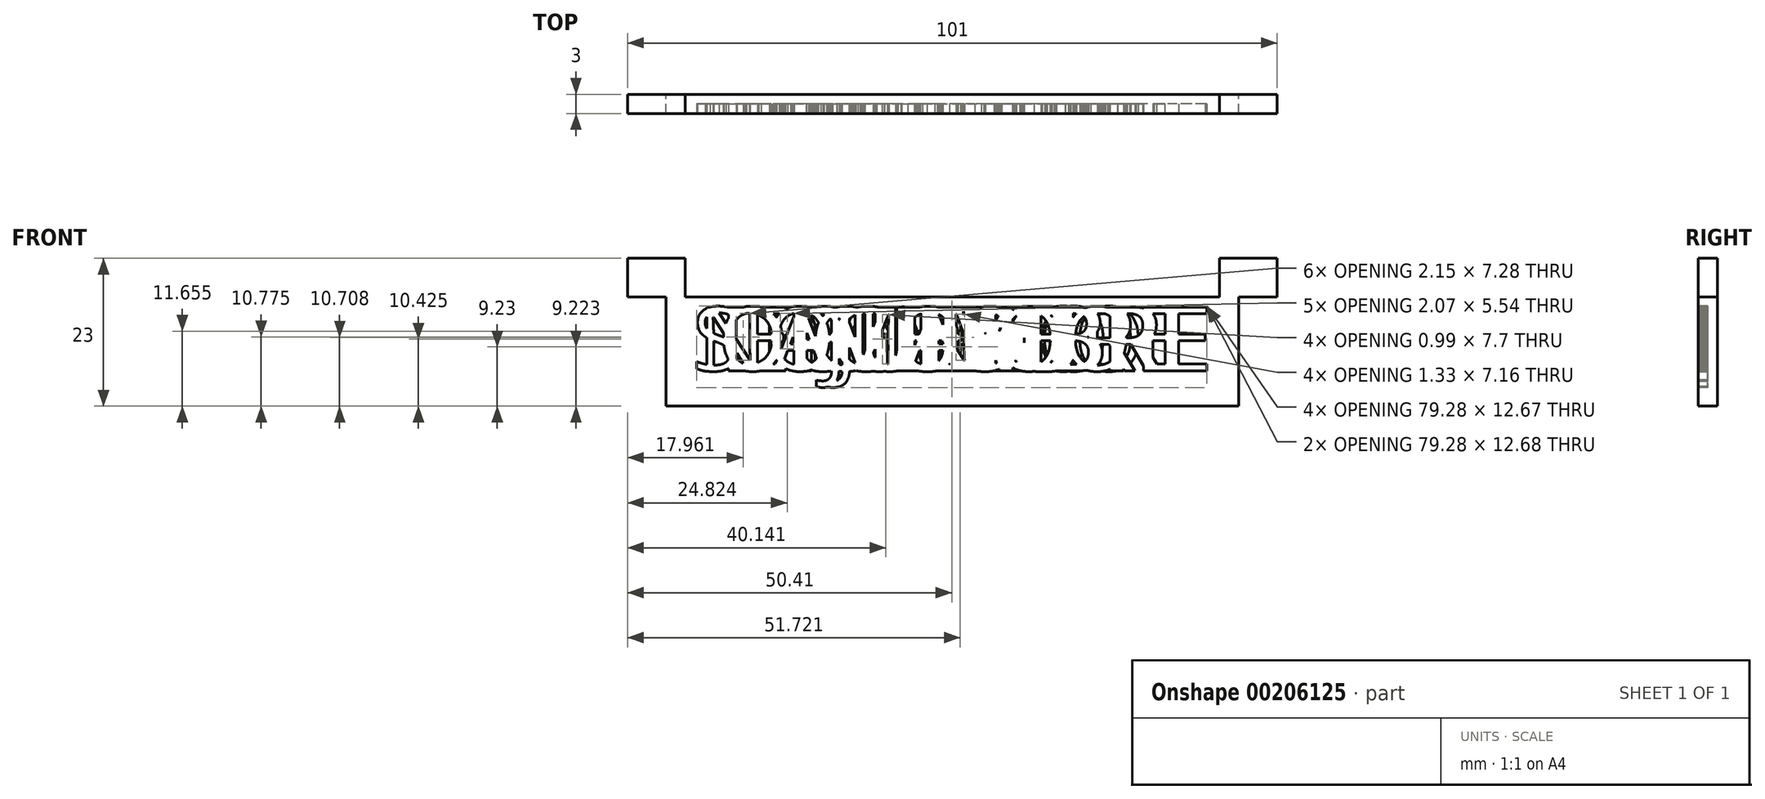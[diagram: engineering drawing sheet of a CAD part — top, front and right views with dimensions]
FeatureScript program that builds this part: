
annotation { "Feature Type Name" : "Feature", "Feature Type Description" : "" }
export const myFeature = defineFeature(function(context is Context, id is Id, definition is map)
    precondition{}
    {
        {
            var Q0;
            Q0=qCreatedBy(makeId("Front.planeOp"),FACE);
            var sketch = newSketch(context, id + "F0", { "sketchPlane" : qUnion([Q0])});
            skLineSegment(sketch, "E0.bottom", {"start": v(-51.5, 23) * mm, "end": v(-42.5, 23) * mm});
            skLineSegment(sketch, "E0.top", {"start": v(-45.5, 0) * mm, "end": v(43.5, 0) * mm});
            skLineSegment(sketch, "E0.left", {"start": v(-51.5, 23) * mm, "end": v(-51.5, 17) * mm});
            skLineSegment(sketch, "E0.right", {"start": v(49.5, 23) * mm, "end": v(49.5, 17) * mm});
            skLineSegment(sketch, "E1.top", {"start": v(-51.5, 17) * mm, "end": v(-45.5, 17) * mm});
            skLineSegment(sketch, "E1.right", {"start": v(-45.5, 0) * mm, "end": v(-45.5, 17) * mm});
            skLineSegment(sketch, "E2.bottom", {"start": v(-51.5, 23) * mm, "end": v(-42.5, 23) * mm, "construction": true});
            skLineSegment(sketch, "E2.top", {"start": v(-51.5, 17) * mm, "end": v(-42.5, 17) * mm, "construction": true});
            skLineSegment(sketch, "E2.left", {"start": v(-51.5, 23) * mm, "end": v(-51.5, 17) * mm, "construction": true});
            skLineSegment(sketch, "E2.right", {"start": v(-42.5, 23) * mm, "end": v(-42.5, 17) * mm, "construction": true});
            skLineSegment(sketch, "E3.top", {"start": v(-42.5, 17) * mm, "end": v(40.5, 17) * mm});
            skLineSegment(sketch, "E3.left", {"start": v(-42.5, 23) * mm, "end": v(-42.5, 17) * mm});
            skLineSegment(sketch, "E3.right", {"start": v(40.5, 23) * mm, "end": v(40.5, 17) * mm});
            skLineSegment(sketch, "E4.top", {"start": v(49.5, 17) * mm, "end": v(43.5, 17) * mm});
            skLineSegment(sketch, "E4.right", {"start": v(43.5, 0) * mm, "end": v(43.5, 17) * mm});
            skLineSegment(sketch, "E5.trimOffspring", {"start": v(40.5, 23) * mm, "end": v(49.5, 23) * mm});
            skSolve(sketch);
        }
        {
            var Q0;
            Q0=makeQuery(id+"F0.imprint","IMPRINT",FACE,{"disambiguationData":[TD([[makeQuery(id+"F0.imprint","IMPRINT",EDGE,{"derivedFrom":sQuery(id+"F0.wireOp",EDGE,"E0.bottom")}),-1.0]])]});
            extrude(context, id + "F1", {"entities" : qUnion([Q0]), "depth" : 3 * mm});
        }
        {
            var Q0;
            Q0=makeQuery(id+"F1.opExtrude","CAP_FACE",FACE,{"disambiguationData":[OSD([sQuery(id+"F0.wireOp",EDGE,"E0.bottom"),sQuery(id+"F0.wireOp",EDGE,"E0.top"),sQuery(id+"F0.wireOp",EDGE,"E0.left"),sQuery(id+"F0.wireOp",EDGE,"E0.right"),sQuery(id+"F0.wireOp",EDGE,"E1.top"),sQuery(id+"F0.wireOp",EDGE,"E1.right"),sQuery(id+"F0.wireOp",EDGE,"E3.top"),sQuery(id+"F0.wireOp",EDGE,"E3.left"),sQuery(id+"F0.wireOp",EDGE,"E3.right"),sQuery(id+"F0.wireOp",EDGE,"E4.top"),sQuery(id+"F0.wireOp",EDGE,"E4.right"),sQuery(id+"F0.wireOp",EDGE,"E5.trimOffspring")])],"isStart":false});
            var sketch = newSketch(context, id + "F2", { "sketchPlane" : qUnion([Q0])});
            skLineSegment(sketch, "E6.0", {"start": v(-45.5, 3.5) * mm, "end": v(-42, 3.5) * mm, "construction": true});
            skLineSegment(sketch, "E7.0", {"start": v(-42, 15.5) * mm, "end": v(40, 15.5) * mm, "construction": true});
            skLineSegment(sketch, "E8.0", {"start": v(-42, 0) * mm, "end": v(-42, 15.5) * mm, "construction": true});
            skText(sketch, "E9", { "text": "ENERO", "fontName": "OpenSans-Regular.ttf"});
            skLineSegment(sketch, "E10.top", {"start": v(-45.5, 0) * mm, "end": v(-42, 0) * mm, "construction": true});
            skLineSegment(sketch, "E10.left", {"start": v(-45.5, 3.5) * mm, "end": v(-45.5, 0) * mm, "construction": true});
            skLineSegment(sketch, "E10.right", {"start": v(-42, 3.5) * mm, "end": v(-42, 0) * mm, "construction": true});
            skLineSegment(sketch, "E11.0", {"start": v(40, 0) * mm, "end": v(40, 17) * mm, "construction": true});
            skPoint(sketch, "E12.orphan", {"position": v(40, 15.5) * mm});
            skPoint(sketch, "E13.end.orphan", {"position": v(-1, 0) * mm});
            skLineSegment(sketch, "E14", {"start": v(-1, 17) * mm, "end": v(-1, 0) * mm, "construction": true});
            const initialGuessF2  = {"E9": [-0.02369, 0.0055, 1, 0, 0.01]};
            skSetInitialGuess(sketch, initialGuessF2);
            skSolve(sketch);
        }
        {
            var Q0;
            Q0=makeQuery(id+"F2.imprint","IMPRINT",FACE,{"disambiguationData":[TD([[makeQuery(id+"F2.imprint","IMPRINT",EDGE,{"derivedFrom":sQuery(id+"F2.wireOp",EDGE,"E9.sketch_text.stroke-0")}),-1.0]])]});
            var Q1;
            Q1=makeQuery(id+"F2.imprint","IMPRINT",FACE,{"disambiguationData":[TD([[makeQuery(id+"F2.imprint","IMPRINT",EDGE,{"derivedFrom":sQuery(id+"F2.wireOp",EDGE,"E9.sketch_text.stroke-10")}),-1.0]])]});
            var Q2;
            Q2=makeQuery(id+"F2.imprint","IMPRINT",FACE,{"disambiguationData":[TD([[makeQuery(id+"F2.imprint","IMPRINT",EDGE,{"derivedFrom":sQuery(id+"F2.wireOp",EDGE,"E9.sketch_text.stroke-23")}),-1.0]])]});
            var Q3;
            Q3=makeQuery(id+"F2.imprint","IMPRINT",FACE,{"disambiguationData":[TD([[makeQuery(id+"F2.imprint","IMPRINT",EDGE,{"derivedFrom":sQuery(id+"F2.wireOp",EDGE,"E9.sketch_text.stroke-38")}),-1.0]])]});
            var Q4;
            Q4=makeQuery(id+"F2.imprint","IMPRINT",FACE,{"disambiguationData":[TD([[makeQuery(id+"F2.imprint","IMPRINT",EDGE,{"derivedFrom":sQuery(id+"F2.wireOp",EDGE,"E9.sketch_text.stroke-52")}),-1.0]])]});
            var Q5;
            Q5=makeQuery(id+"F2.imprint","IMPRINT",FACE,{"disambiguationData":[TD([[makeQuery(id+"F2.imprint","IMPRINT",EDGE,{"derivedFrom":sQuery(id+"F2.wireOp",EDGE,"E9.sketch_text.stroke-65")}),-1.0]])]});
            var Q6;
            Q6=makeQuery(id+"F2.imprint","IMPRINT",FACE,{"disambiguationData":[TD([[makeQuery(id+"F2.imprint","IMPRINT",EDGE,{"derivedFrom":sQuery(id+"F2.wireOp",EDGE,"E9.sketch_text.stroke-83")}),-1.0]])]});
            extrude(context, id + "F3", {"entities" : qUnion([Q0, Q1, Q2, Q3, Q4, Q5, Q6]), "operationType" : NewBodyOperationType.REMOVE, "oppositeDirection" : true, "depth" : 1.5 * mm});
        }
        {
            var Q0;
            Q0=qSketchRegion(id+"F0",true);
            extrude(context, id + "F4", {"entities" : qUnion([Q0]), "depth" : 3 * mm});
        }
        {
            var Q0;
            Q0=makeQuery(id+"F4.opExtrude","CAP_FACE",FACE,{"disambiguationData":[OSD([sQuery(id+"F0.wireOp",EDGE,"E0.bottom"),sQuery(id+"F0.wireOp",EDGE,"E0.top"),sQuery(id+"F0.wireOp",EDGE,"E0.left"),sQuery(id+"F0.wireOp",EDGE,"E0.right"),sQuery(id+"F0.wireOp",EDGE,"E1.top"),sQuery(id+"F0.wireOp",EDGE,"E1.right"),sQuery(id+"F0.wireOp",EDGE,"E3.top"),sQuery(id+"F0.wireOp",EDGE,"E3.left"),sQuery(id+"F0.wireOp",EDGE,"E3.right"),sQuery(id+"F0.wireOp",EDGE,"E4.top"),sQuery(id+"F0.wireOp",EDGE,"E4.right"),sQuery(id+"F0.wireOp",EDGE,"E5.trimOffspring")])],"isStart":false});
            var sketch = newSketch(context, id + "F5", { "sketchPlane" : qUnion([Q0])});
            skText(sketch, "E15", { "text": "FEBRERO", "fontName": "OpenSans-Regular.ttf"});
            skPoint(sketch, "E16.orphan", {"position": v(40.22, 15.5) * mm});
            skPoint(sketch, "E17.end.orphan", {"position": v(-0.5, 0) * mm});
            skPoint(sketch, "E18.orphan", {"position": v(-42.22, 15.5) * mm});
            skLineSegment(sketch, "E19.0", {"start": v(-43.5, 15.5) * mm, "end": v(41.5, 15.5) * mm, "construction": true});
            skPoint(sketch, "E20.start.orphan", {"position": v(-1, 17) * mm});
            const initialGuessF5  = {"E15": [-0.03083, 0.0055, 1, 0, 0.01]};
            skSetInitialGuess(sketch, initialGuessF5);
            skSolve(sketch);
        }
        {
            var Q0;
            Q0=makeQuery(id+"F5.imprint","IMPRINT",FACE,{"disambiguationData":[TD([[makeQuery(id+"F5.imprint","IMPRINT",EDGE,{"derivedFrom":sQuery(id+"F5.wireOp",EDGE,"E15.sketch_text.stroke-0")}),-1.0]])]});
            var Q1;
            Q1=makeQuery(id+"F5.imprint","IMPRINT",FACE,{"disambiguationData":[TD([[makeQuery(id+"F5.imprint","IMPRINT",EDGE,{"derivedFrom":sQuery(id+"F5.wireOp",EDGE,"E15.sketch_text.stroke-10")}),-1.0]])]});
            var Q2;
            Q2=makeQuery(id+"F5.imprint","IMPRINT",FACE,{"disambiguationData":[TD([[makeQuery(id+"F5.imprint","IMPRINT",EDGE,{"derivedFrom":sQuery(id+"F5.wireOp",EDGE,"E15.sketch_text.stroke-22")}),-1.0]])]});
            var Q3;
            Q3=makeQuery(id+"F5.imprint","IMPRINT",FACE,{"disambiguationData":[TD([[makeQuery(id+"F5.imprint","IMPRINT",EDGE,{"derivedFrom":sQuery(id+"F5.wireOp",EDGE,"E15.sketch_text.stroke-47")}),-1.0]])]});
            var Q4;
            Q4=makeQuery(id+"F5.imprint","IMPRINT",FACE,{"disambiguationData":[TD([[makeQuery(id+"F5.imprint","IMPRINT",EDGE,{"derivedFrom":sQuery(id+"F5.wireOp",EDGE,"E15.sketch_text.stroke-65")}),-1.0]])]});
            var Q5;
            Q5=makeQuery(id+"F5.imprint","IMPRINT",FACE,{"disambiguationData":[TD([[makeQuery(id+"F5.imprint","IMPRINT",EDGE,{"derivedFrom":sQuery(id+"F5.wireOp",EDGE,"E15.sketch_text.stroke-79")}),-1.0]])]});
            var Q6;
            Q6=makeQuery(id+"F5.imprint","IMPRINT",FACE,{"disambiguationData":[TD([[makeQuery(id+"F5.imprint","IMPRINT",EDGE,{"derivedFrom":sQuery(id+"F5.wireOp",EDGE,"E15.sketch_text.stroke-92")}),-1.0]])]});
            var Q7;
            Q7=makeQuery(id+"F5.imprint","IMPRINT",FACE,{"disambiguationData":[TD([[makeQuery(id+"F5.imprint","IMPRINT",EDGE,{"derivedFrom":sQuery(id+"F5.wireOp",EDGE,"E15.sketch_text.stroke-110")}),-1.0]])]});
            extrude(context, id + "F6", {"entities" : qUnion([Q0, Q1, Q2, Q3, Q4, Q5, Q6, Q7]), "operationType" : NewBodyOperationType.REMOVE, "oppositeDirection" : true, "depth" : 1.5 * mm});
        }
        {
            var Q0;
            Q0=makeQuery(id+"F0.imprint","IMPRINT",FACE,{"disambiguationData":[TD([[makeQuery(id+"F0.imprint","IMPRINT",EDGE,{"derivedFrom":sQuery(id+"F0.wireOp",EDGE,"E0.bottom")}),-1.0]])]});
            extrude(context, id + "F7", {"entities" : qUnion([Q0]), "depth" : 3 * mm});
        }
        {
            var Q0;
            Q0=makeQuery(id+"F7.opExtrude","CAP_FACE",FACE,{"disambiguationData":[OSD([sQuery(id+"F0.wireOp",EDGE,"E0.bottom"),sQuery(id+"F0.wireOp",EDGE,"E0.top"),sQuery(id+"F0.wireOp",EDGE,"E0.left"),sQuery(id+"F0.wireOp",EDGE,"E0.right"),sQuery(id+"F0.wireOp",EDGE,"E1.top"),sQuery(id+"F0.wireOp",EDGE,"E1.right"),sQuery(id+"F0.wireOp",EDGE,"E3.top"),sQuery(id+"F0.wireOp",EDGE,"E3.left"),sQuery(id+"F0.wireOp",EDGE,"E3.right"),sQuery(id+"F0.wireOp",EDGE,"E4.top"),sQuery(id+"F0.wireOp",EDGE,"E4.right"),sQuery(id+"F0.wireOp",EDGE,"E5.trimOffspring")])],"isStart":false});
            var sketch = newSketch(context, id + "F8", { "sketchPlane" : qUnion([Q0])});
            skText(sketch, "E21", { "text": "MARZO", "fontName": "OpenSans-Regular.ttf"});
            skPoint(sketch, "E22.orphan", {"position": v(34.75, 15.5) * mm});
            skPoint(sketch, "E23.end.orphan", {"position": v(0, -12.7) * mm});
            skPoint(sketch, "E24.orphan", {"position": v(-36.75, 15.5) * mm});
            skPoint(sketch, "E25.start.orphan", {"position": v(0, 4.3) * mm});
            skLineSegment(sketch, "E26.0", {"start": v(-43.5, 15.5) * mm, "end": v(41.5, 15.5) * mm, "construction": true});
            const initialGuessF8  = {"E21": [-0.02536, 0.0055, 1, 0, 0.01]};
            skSetInitialGuess(sketch, initialGuessF8);
            skSolve(sketch);
        }
        {
            var Q0;
            Q0=makeQuery(id+"F8.imprint","IMPRINT",FACE,{"disambiguationData":[TD([[makeQuery(id+"F8.imprint","IMPRINT",EDGE,{"derivedFrom":sQuery(id+"F8.wireOp",EDGE,"E21.sketch_text.stroke-0")}),-1.0]])]});
            var Q1;
            Q1=makeQuery(id+"F8.imprint","IMPRINT",FACE,{"disambiguationData":[TD([[makeQuery(id+"F8.imprint","IMPRINT",EDGE,{"derivedFrom":sQuery(id+"F8.wireOp",EDGE,"E21.sketch_text.stroke-18")}),-1.0]])]});
            var Q2;
            Q2=makeQuery(id+"F8.imprint","IMPRINT",FACE,{"disambiguationData":[TD([[makeQuery(id+"F8.imprint","IMPRINT",EDGE,{"derivedFrom":sQuery(id+"F8.wireOp",EDGE,"E21.sketch_text.stroke-31")}),-1.0]])]});
            var Q3;
            Q3=makeQuery(id+"F8.imprint","IMPRINT",FACE,{"disambiguationData":[TD([[makeQuery(id+"F8.imprint","IMPRINT",EDGE,{"derivedFrom":sQuery(id+"F8.wireOp",EDGE,"E21.sketch_text.stroke-49")}),-1.0]])]});
            var Q4;
            Q4=makeQuery(id+"F8.imprint","IMPRINT",FACE,{"disambiguationData":[TD([[makeQuery(id+"F8.imprint","IMPRINT",EDGE,{"derivedFrom":sQuery(id+"F8.wireOp",EDGE,"E21.sketch_text.stroke-64")}),-1.0]])]});
            extrude(context, id + "F9", {"entities" : qUnion([Q0, Q1, Q2, Q3, Q4]), "operationType" : NewBodyOperationType.REMOVE, "oppositeDirection" : true, "depth" : 1.5 * mm});
        }
        {
            var Q0;
            Q0=makeQuery(id+"F0.imprint","IMPRINT",FACE,{"disambiguationData":[TD([[makeQuery(id+"F0.imprint","IMPRINT",EDGE,{"derivedFrom":sQuery(id+"F0.wireOp",EDGE,"E0.bottom")}),-1.0]])]});
            extrude(context, id + "F10", {"entities" : qUnion([Q0]), "depth" : 3 * mm});
        }
        {
            var Q0;
            Q0=makeQuery(id+"F10.opExtrude","CAP_FACE",FACE,{"disambiguationData":[OSD([sQuery(id+"F0.wireOp",EDGE,"E0.bottom"),sQuery(id+"F0.wireOp",EDGE,"E0.top"),sQuery(id+"F0.wireOp",EDGE,"E0.left"),sQuery(id+"F0.wireOp",EDGE,"E0.right"),sQuery(id+"F0.wireOp",EDGE,"E1.top"),sQuery(id+"F0.wireOp",EDGE,"E1.right"),sQuery(id+"F0.wireOp",EDGE,"E3.top"),sQuery(id+"F0.wireOp",EDGE,"E3.left"),sQuery(id+"F0.wireOp",EDGE,"E3.right"),sQuery(id+"F0.wireOp",EDGE,"E4.top"),sQuery(id+"F0.wireOp",EDGE,"E4.right"),sQuery(id+"F0.wireOp",EDGE,"E5.trimOffspring")])],"isStart":false});
            var sketch = newSketch(context, id + "F11", { "sketchPlane" : qUnion([Q0])});
            skText(sketch, "E27", { "text": "ABRIL", "fontName": "OpenSans-Regular.ttf"});
            skPoint(sketch, "E28.orphan", {"position": v(29.4, 15.5) * mm});
            skPoint(sketch, "E29.end.orphan", {"position": v(0.3, -20.32) * mm});
            skPoint(sketch, "E30.orphan", {"position": v(-31.4, 15.5) * mm});
            skPoint(sketch, "E31.start.orphan", {"position": v(0.3, -3.32) * mm});
            skLineSegment(sketch, "E32.0", {"start": v(-43.5, 15.5) * mm, "end": v(41.5, 15.5) * mm});
            const initialGuessF11  = {"E27": [-0.02002, 0.0055, 1, 0, 0.01]};
            skSetInitialGuess(sketch, initialGuessF11);
            skSolve(sketch);
        }
        {
            var Q0;
            Q0=makeQuery(id+"F11.imprint","IMPRINT",FACE,{"disambiguationData":[TD([[makeQuery(id+"F11.imprint","IMPRINT",EDGE,{"derivedFrom":sQuery(id+"F11.wireOp",EDGE,"E27.sketch_text.stroke-0")}),-1.0]])]});
            var Q1;
            Q1=makeQuery(id+"F11.imprint","IMPRINT",FACE,{"disambiguationData":[TD([[makeQuery(id+"F11.imprint","IMPRINT",EDGE,{"derivedFrom":sQuery(id+"F11.wireOp",EDGE,"E27.sketch_text.stroke-13")}),-1.0]])]});
            var Q2;
            Q2=makeQuery(id+"F11.imprint","IMPRINT",FACE,{"disambiguationData":[TD([[makeQuery(id+"F11.imprint","IMPRINT",EDGE,{"derivedFrom":sQuery(id+"F11.wireOp",EDGE,"E27.sketch_text.stroke-28")}),-1.0]])]});
            var Q3;
            Q3=makeQuery(id+"F11.imprint","IMPRINT",FACE,{"disambiguationData":[TD([[makeQuery(id+"F11.imprint","IMPRINT",EDGE,{"derivedFrom":sQuery(id+"F11.wireOp",EDGE,"E27.sketch_text.stroke-46")}),-1.0]])]});
            var Q4;
            Q4=makeQuery(id+"F11.imprint","IMPRINT",FACE,{"disambiguationData":[TD([[makeQuery(id+"F11.imprint","IMPRINT",EDGE,{"derivedFrom":sQuery(id+"F11.wireOp",EDGE,"E27.sketch_text.stroke-50")}),-1.0]])]});
            var Q5;
            Q5=makeQuery(id+"F11.imprint","IMPRINT",FACE,{"disambiguationData":[TD([[makeQuery(id+"F11.imprint","IMPRINT",EDGE,{"derivedFrom":sQuery(id+"F11.wireOp",EDGE,"E27.sketch_text.stroke-56")}),-1.0]])]});
            var Q6;
            Q6=makeQuery(id+"F11.imprint","IMPRINT",FACE,{"disambiguationData":[TD([[makeQuery(id+"F11.imprint","IMPRINT",EDGE,{"derivedFrom":sQuery(id+"F11.wireOp",EDGE,"E27.sketch_text.stroke-60")}),-1.0]])]});
            extrude(context, id + "F12", {"entities" : qUnion([Q0, Q1, Q2, Q3, Q4, Q5, Q6]), "operationType" : NewBodyOperationType.REMOVE, "oppositeDirection" : true, "depth" : 1.5 * mm});
        }
        {
            var Q0;
            Q0=makeQuery(id+"F0.imprint","IMPRINT",FACE,{"disambiguationData":[TD([[makeQuery(id+"F0.imprint","IMPRINT",EDGE,{"derivedFrom":sQuery(id+"F0.wireOp",EDGE,"E0.bottom")}),-1.0]])]});
            extrude(context, id + "F13", {"entities" : qUnion([Q0]), "depth" : 3 * mm});
        }
        {
            var Q0;
            Q0=makeQuery(id+"F13.opExtrude","CAP_FACE",FACE,{"disambiguationData":[OSD([sQuery(id+"F0.wireOp",EDGE,"E0.bottom"),sQuery(id+"F0.wireOp",EDGE,"E0.top"),sQuery(id+"F0.wireOp",EDGE,"E0.left"),sQuery(id+"F0.wireOp",EDGE,"E0.right"),sQuery(id+"F0.wireOp",EDGE,"E1.top"),sQuery(id+"F0.wireOp",EDGE,"E1.right"),sQuery(id+"F0.wireOp",EDGE,"E3.top"),sQuery(id+"F0.wireOp",EDGE,"E3.left"),sQuery(id+"F0.wireOp",EDGE,"E3.right"),sQuery(id+"F0.wireOp",EDGE,"E4.top"),sQuery(id+"F0.wireOp",EDGE,"E4.right"),sQuery(id+"F0.wireOp",EDGE,"E5.trimOffspring")])],"isStart":false});
            var sketch = newSketch(context, id + "F14", { "sketchPlane" : qUnion([Q0])});
            skText(sketch, "E33", { "text": "MAYO", "fontName": "OpenSans-Regular.ttf"});
            skPoint(sketch, "E34.orphan", {"position": v(30.38, 15.5) * mm});
            skPoint(sketch, "E35.end.orphan", {"position": v(0.48, -24.9) * mm});
            skPoint(sketch, "E36.orphan", {"position": v(-32.38, 15.5) * mm});
            skPoint(sketch, "E37.start.orphan", {"position": v(0.48, -7.9) * mm});
            skLineSegment(sketch, "E38.0", {"start": v(-45.29, 15.5) * mm, "end": v(43.29, 15.5) * mm});
            skLineSegment(sketch, "E39.0", {"start": v(-43.5, 15.5) * mm, "end": v(41.5, 15.5) * mm});
            const initialGuessF14  = {"E33": [-0.02099, 0.0055, 1, 0, 0.01]};
            skSetInitialGuess(sketch, initialGuessF14);
            skSolve(sketch);
        }
        {
            var Q0;
            Q0=makeQuery(id+"F0.imprint","IMPRINT",FACE,{"disambiguationData":[TD([[makeQuery(id+"F0.imprint","IMPRINT",EDGE,{"derivedFrom":sQuery(id+"F0.wireOp",EDGE,"E0.bottom")}),-1.0]])]});
            extrude(context, id + "F15", {"entities" : qUnion([Q0]), "depth" : 3 * mm});
        }
        {
            var Q0;
            Q0=makeQuery(id+"F15.opExtrude","CAP_FACE",FACE,{"disambiguationData":[OSD([sQuery(id+"F0.wireOp",EDGE,"E0.bottom"),sQuery(id+"F0.wireOp",EDGE,"E0.top"),sQuery(id+"F0.wireOp",EDGE,"E0.left"),sQuery(id+"F0.wireOp",EDGE,"E0.right"),sQuery(id+"F0.wireOp",EDGE,"E1.top"),sQuery(id+"F0.wireOp",EDGE,"E1.right"),sQuery(id+"F0.wireOp",EDGE,"E3.top"),sQuery(id+"F0.wireOp",EDGE,"E3.left"),sQuery(id+"F0.wireOp",EDGE,"E3.right"),sQuery(id+"F0.wireOp",EDGE,"E4.top"),sQuery(id+"F0.wireOp",EDGE,"E4.right"),sQuery(id+"F0.wireOp",EDGE,"E5.trimOffspring")])],"isStart":false});
            var sketch = newSketch(context, id + "F16", { "sketchPlane" : qUnion([Q0])});
            skText(sketch, "E40", { "text": "JUNIO", "fontName": "OpenSans-Regular.ttf"});
            skPoint(sketch, "E41.orphan", {"position": v(30.45, 15.5) * mm});
            skPoint(sketch, "E42.end.orphan", {"position": v(0.65, -29.76) * mm});
            skPoint(sketch, "E43.orphan", {"position": v(-32.45, 15.5) * mm});
            skPoint(sketch, "E44.start.orphan", {"position": v(0.65, -12.76) * mm});
            skLineSegment(sketch, "E45.0", {"start": v(-45.36, 15.5) * mm, "end": v(43.36, 15.5) * mm});
            skLineSegment(sketch, "E46.0", {"start": v(-49.06, 15.5) * mm, "end": v(47.06, 15.5) * mm});
            skLineSegment(sketch, "E47.0", {"start": v(-43.5, 15.5) * mm, "end": v(41.5, 15.5) * mm});
            const initialGuessF16  = {"E40": [-0.02106, 0.0055, 1, 0, 0.01]};
            skSetInitialGuess(sketch, initialGuessF16);
            skSolve(sketch);
        }
        {
            var Q0;
            Q0=makeQuery(id+"F0.imprint","IMPRINT",FACE,{"disambiguationData":[TD([[makeQuery(id+"F0.imprint","IMPRINT",EDGE,{"derivedFrom":sQuery(id+"F0.wireOp",EDGE,"E0.bottom")}),-1.0]])]});
            extrude(context, id + "F17", {"entities" : qUnion([Q0]), "depth" : 3 * mm});
        }
        {
            var Q0;
            Q0=makeQuery(id+"F17.opExtrude","CAP_FACE",FACE,{"disambiguationData":[OSD([sQuery(id+"F0.wireOp",EDGE,"E0.bottom"),sQuery(id+"F0.wireOp",EDGE,"E0.top"),sQuery(id+"F0.wireOp",EDGE,"E0.left"),sQuery(id+"F0.wireOp",EDGE,"E0.right"),sQuery(id+"F0.wireOp",EDGE,"E1.top"),sQuery(id+"F0.wireOp",EDGE,"E1.right"),sQuery(id+"F0.wireOp",EDGE,"E3.top"),sQuery(id+"F0.wireOp",EDGE,"E3.left"),sQuery(id+"F0.wireOp",EDGE,"E3.right"),sQuery(id+"F0.wireOp",EDGE,"E4.top"),sQuery(id+"F0.wireOp",EDGE,"E4.right"),sQuery(id+"F0.wireOp",EDGE,"E5.trimOffspring")])],"isStart":false});
            var sketch = newSketch(context, id + "F18", { "sketchPlane" : qUnion([Q0])});
            skText(sketch, "E48", { "text": "JULIO", "fontName": "OpenSans-Regular.ttf"});
            skPoint(sketch, "E49.orphan", {"position": v(28.82, 15.5) * mm});
            skPoint(sketch, "E50.end.orphan", {"position": v(0.82, -34.76) * mm});
            skPoint(sketch, "E51.orphan", {"position": v(-30.82, 15.5) * mm});
            skPoint(sketch, "E52.start.orphan", {"position": v(0.82, -17.76) * mm});
            skLineSegment(sketch, "E53.0", {"start": v(-43.73, 15.5) * mm, "end": v(41.73, 15.5) * mm});
            skLineSegment(sketch, "E54.0", {"start": v(-47.42, 15.5) * mm, "end": v(45.42, 15.5) * mm});
            skLineSegment(sketch, "E55.0", {"start": v(-45.84, 15.5) * mm, "end": v(43.84, 15.5) * mm});
            skLineSegment(sketch, "E56.0", {"start": v(-43.5, 15.5) * mm, "end": v(41.5, 15.5) * mm});
            const initialGuessF18  = {"E48": [-0.01943, 0.0055, 1, 0, 0.01]};
            skSetInitialGuess(sketch, initialGuessF18);
            skSolve(sketch);
        }
        {
            var Q0;
            Q0=makeQuery(id+"F0.imprint","IMPRINT",FACE,{"disambiguationData":[TD([[makeQuery(id+"F0.imprint","IMPRINT",EDGE,{"derivedFrom":sQuery(id+"F0.wireOp",EDGE,"E0.bottom")}),-1.0]])]});
            extrude(context, id + "F19", {"entities" : qUnion([Q0]), "depth" : 3 * mm});
        }
        {
            var Q0;
            Q0=makeQuery(id+"F19.opExtrude","CAP_FACE",FACE,{"disambiguationData":[OSD([sQuery(id+"F0.wireOp",EDGE,"E0.bottom"),sQuery(id+"F0.wireOp",EDGE,"E0.top"),sQuery(id+"F0.wireOp",EDGE,"E0.left"),sQuery(id+"F0.wireOp",EDGE,"E0.right"),sQuery(id+"F0.wireOp",EDGE,"E1.top"),sQuery(id+"F0.wireOp",EDGE,"E1.right"),sQuery(id+"F0.wireOp",EDGE,"E3.top"),sQuery(id+"F0.wireOp",EDGE,"E3.left"),sQuery(id+"F0.wireOp",EDGE,"E3.right"),sQuery(id+"F0.wireOp",EDGE,"E4.top"),sQuery(id+"F0.wireOp",EDGE,"E4.right"),sQuery(id+"F0.wireOp",EDGE,"E5.trimOffspring")])],"isStart":false});
            var sketch = newSketch(context, id + "F20", { "sketchPlane" : qUnion([Q0])});
            skText(sketch, "E57", { "text": "AGOSTO", "fontName": "OpenSans-Regular.ttf"});
            skPoint(sketch, "E58.orphan", {"position": v(38.34, 15.5) * mm});
            skPoint(sketch, "E59.end.orphan", {"position": v(1, -39.82) * mm});
            skPoint(sketch, "E60.orphan", {"position": v(-40.34, 15.5) * mm});
            skPoint(sketch, "E61.start.orphan", {"position": v(1, -22.82) * mm});
            skLineSegment(sketch, "E62.0", {"start": v(-53.25, 15.5) * mm, "end": v(51.25, 15.5) * mm});
            skLineSegment(sketch, "E63.0", {"start": v(-56.94, 15.5) * mm, "end": v(54.94, 15.5) * mm});
            skLineSegment(sketch, "E64.0", {"start": v(-55.36, 15.5) * mm, "end": v(53.36, 15.5) * mm});
            skLineSegment(sketch, "E65.0", {"start": v(-56.55, 15.5) * mm, "end": v(54.55, 15.5) * mm});
            skLineSegment(sketch, "E66.0", {"start": v(-43.5, 15.5) * mm, "end": v(41.5, 15.5) * mm});
            const initialGuessF20  = {"E57": [-0.02895, 0.0055, 1, 0, 0.01]};
            skSetInitialGuess(sketch, initialGuessF20);
            skSolve(sketch);
        }
        {
            var Q0;
            Q0=makeQuery(id+"F0.imprint","IMPRINT",FACE,{"disambiguationData":[TD([[makeQuery(id+"F0.imprint","IMPRINT",EDGE,{"derivedFrom":sQuery(id+"F0.wireOp",EDGE,"E0.bottom")}),-1.0]])]});
            extrude(context, id + "F21", {"entities" : qUnion([Q0]), "depth" : 3 * mm});
        }
        {
            var Q0;
            Q0=makeQuery(id+"F21.opExtrude","CAP_FACE",FACE,{"disambiguationData":[OSD([sQuery(id+"F0.wireOp",EDGE,"E0.bottom"),sQuery(id+"F0.wireOp",EDGE,"E0.top"),sQuery(id+"F0.wireOp",EDGE,"E0.left"),sQuery(id+"F0.wireOp",EDGE,"E0.right"),sQuery(id+"F0.wireOp",EDGE,"E1.top"),sQuery(id+"F0.wireOp",EDGE,"E1.right"),sQuery(id+"F0.wireOp",EDGE,"E3.top"),sQuery(id+"F0.wireOp",EDGE,"E3.left"),sQuery(id+"F0.wireOp",EDGE,"E3.right"),sQuery(id+"F0.wireOp",EDGE,"E4.top"),sQuery(id+"F0.wireOp",EDGE,"E4.right"),sQuery(id+"F0.wireOp",EDGE,"E5.trimOffspring")])],"isStart":false});
            var sketch = newSketch(context, id + "F22", { "sketchPlane" : qUnion([Q0])});
            skText(sketch, "E67", { "text": "SEPTIEMBRE", "fontName": "OpenSans-Regular.ttf"});
            skPoint(sketch, "E68.orphan", {"position": v(50.84, 15.5) * mm});
            skPoint(sketch, "E69.end.orphan", {"position": v(1.16, -44.91) * mm});
            skPoint(sketch, "E70.orphan", {"position": v(-52.84, 15.5) * mm});
            skPoint(sketch, "E71.start.orphan", {"position": v(1.16, -27.91) * mm});
            const initialGuessF22  = {"E67": [-0.04145, 0.0055, 1, 0, 0.01]};
            skSetInitialGuess(sketch, initialGuessF22);
            skSolve(sketch);
        }
        {
            var Q0;
            Q0=makeQuery(id+"F0.imprint","IMPRINT",FACE,{"disambiguationData":[TD([[makeQuery(id+"F0.imprint","IMPRINT",EDGE,{"derivedFrom":sQuery(id+"F0.wireOp",EDGE,"E0.bottom")}),-1.0]])]});
            extrude(context, id + "F23", {"entities" : qUnion([Q0]), "depth" : 3 * mm});
        }
        {
            var Q0;
            Q0=makeQuery(id+"F23.opExtrude","CAP_FACE",FACE,{"disambiguationData":[OSD([sQuery(id+"F0.wireOp",EDGE,"E0.bottom"),sQuery(id+"F0.wireOp",EDGE,"E0.top"),sQuery(id+"F0.wireOp",EDGE,"E0.left"),sQuery(id+"F0.wireOp",EDGE,"E0.right"),sQuery(id+"F0.wireOp",EDGE,"E1.top"),sQuery(id+"F0.wireOp",EDGE,"E1.right"),sQuery(id+"F0.wireOp",EDGE,"E3.top"),sQuery(id+"F0.wireOp",EDGE,"E3.left"),sQuery(id+"F0.wireOp",EDGE,"E3.right"),sQuery(id+"F0.wireOp",EDGE,"E4.top"),sQuery(id+"F0.wireOp",EDGE,"E4.right"),sQuery(id+"F0.wireOp",EDGE,"E5.trimOffspring")])],"isStart":false});
            var sketch = newSketch(context, id + "F24", { "sketchPlane" : qUnion([Q0])});
            skText(sketch, "E72", { "text": "OCTUBURE", "fontName": "OpenSans-Regular.ttf"});
            skPoint(sketch, "E73.orphan", {"position": v(46.82, 15.5) * mm});
            skPoint(sketch, "E74.end.orphan", {"position": v(1.08, -34.46) * mm});
            skPoint(sketch, "E75.orphan", {"position": v(-48.82, 15.5) * mm});
            skPoint(sketch, "E76.start.orphan", {"position": v(1.08, -17.46) * mm});
            skLineSegment(sketch, "E77.0", {"start": v(-42.5, 15.5) * mm, "end": v(40.5, 15.5) * mm});
            const initialGuessF24  = {"E72": [-0.03743, 0.0055, 1, 0, 0.01]};
            skSetInitialGuess(sketch, initialGuessF24);
            skSolve(sketch);
        }
        {
            var Q0;
            Q0=makeQuery(id+"F0.imprint","IMPRINT",FACE,{"disambiguationData":[TD([[makeQuery(id+"F0.imprint","IMPRINT",EDGE,{"derivedFrom":sQuery(id+"F0.wireOp",EDGE,"E0.bottom")}),-1.0]])]});
            extrude(context, id + "F25", {"entities" : qUnion([Q0]), "depth" : 3 * mm});
        }
        {
            var Q0;
            Q0=makeQuery(id+"F25.opExtrude","CAP_FACE",FACE,{"disambiguationData":[OSD([sQuery(id+"F0.wireOp",EDGE,"E0.bottom"),sQuery(id+"F0.wireOp",EDGE,"E0.top"),sQuery(id+"F0.wireOp",EDGE,"E0.left"),sQuery(id+"F0.wireOp",EDGE,"E0.right"),sQuery(id+"F0.wireOp",EDGE,"E1.top"),sQuery(id+"F0.wireOp",EDGE,"E1.right"),sQuery(id+"F0.wireOp",EDGE,"E3.top"),sQuery(id+"F0.wireOp",EDGE,"E3.left"),sQuery(id+"F0.wireOp",EDGE,"E3.right"),sQuery(id+"F0.wireOp",EDGE,"E4.top"),sQuery(id+"F0.wireOp",EDGE,"E4.right"),sQuery(id+"F0.wireOp",EDGE,"E5.trimOffspring")])],"isStart":false});
            var sketch = newSketch(context, id + "F26", { "sketchPlane" : qUnion([Q0])});
            skText(sketch, "E78", { "text": "NOVIEMBRE", "fontName": "OpenSans-Regular.ttf"});
            skPoint(sketch, "E79.orphan", {"position": v(49.92, 15.5) * mm});
            skPoint(sketch, "E80.end.orphan", {"position": v(1.08, -34.46) * mm});
            skPoint(sketch, "E81.orphan", {"position": v(-51.92, 15.5) * mm});
            skPoint(sketch, "E82.start.orphan", {"position": v(1.08, -17.46) * mm});
            skLineSegment(sketch, "E83.0", {"start": v(-42.5, 15.5) * mm, "end": v(40.5, 15.5) * mm});
            const initialGuessF26  = {"E78": [-0.04053, 0.0055, 1, 0, 0.01]};
            skSetInitialGuess(sketch, initialGuessF26);
            skSolve(sketch);
        }
        {
            var Q0;
            Q0=makeQuery(id+"F0.imprint","IMPRINT",FACE,{"disambiguationData":[TD([[makeQuery(id+"F0.imprint","IMPRINT",EDGE,{"derivedFrom":sQuery(id+"F0.wireOp",EDGE,"E0.bottom")}),-1.0]])]});
            extrude(context, id + "F27", {"entities" : qUnion([Q0]), "depth" : 3 * mm});
        }
        {
            var Q0;
            Q0=makeQuery(id+"F27.opExtrude","CAP_FACE",FACE,{"disambiguationData":[OSD([sQuery(id+"F0.wireOp",EDGE,"E0.bottom"),sQuery(id+"F0.wireOp",EDGE,"E0.top"),sQuery(id+"F0.wireOp",EDGE,"E0.left"),sQuery(id+"F0.wireOp",EDGE,"E0.right"),sQuery(id+"F0.wireOp",EDGE,"E1.top"),sQuery(id+"F0.wireOp",EDGE,"E1.right"),sQuery(id+"F0.wireOp",EDGE,"E3.top"),sQuery(id+"F0.wireOp",EDGE,"E3.left"),sQuery(id+"F0.wireOp",EDGE,"E3.right"),sQuery(id+"F0.wireOp",EDGE,"E4.top"),sQuery(id+"F0.wireOp",EDGE,"E4.right"),sQuery(id+"F0.wireOp",EDGE,"E5.trimOffspring")])],"isStart":false});
            var sketch = newSketch(context, id + "F28", { "sketchPlane" : qUnion([Q0])});
            skText(sketch, "E84", { "text": "DICIEMBRE", "fontName": "OpenSans-Regular.ttf"});
            skPoint(sketch, "E85.orphan", {"position": v(46.53, 15.5) * mm});
            skPoint(sketch, "E86.end.orphan", {"position": v(1.08, -34.46) * mm});
            skPoint(sketch, "E87.orphan", {"position": v(-48.53, 15.5) * mm});
            skPoint(sketch, "E88.start.orphan", {"position": v(1.08, -17.46) * mm});
            skLineSegment(sketch, "E89.0", {"start": v(-42.5, 15.5) * mm, "end": v(40.5, 15.5) * mm});
            const initialGuessF28  = {"E84": [-0.03713, 0.0055, 1, 0, 0.01]};
            skSetInitialGuess(sketch, initialGuessF28);
            skSolve(sketch);
        }
        {
            var Q0;
            Q0=makeQuery(id+"F28.imprint","IMPRINT",FACE,{"disambiguationData":[TD([[makeQuery(id+"F28.imprint","IMPRINT",EDGE,{"derivedFrom":sQuery(id+"F28.wireOp",EDGE,"E84.sketch_text.stroke-0")}),-1.0]])]});
            var Q1;
            Q1=makeQuery(id+"F28.imprint","IMPRINT",FACE,{"disambiguationData":[TD([[makeQuery(id+"F28.imprint","IMPRINT",EDGE,{"derivedFrom":sQuery(id+"F28.wireOp",EDGE,"E84.sketch_text.stroke-14")}),-1.0]])]});
            var Q2;
            Q2=makeQuery(id+"F28.imprint","IMPRINT",FACE,{"disambiguationData":[TD([[makeQuery(id+"F28.imprint","IMPRINT",EDGE,{"derivedFrom":sQuery(id+"F28.wireOp",EDGE,"E84.sketch_text.stroke-26")}),-1.0]])]});
            var Q3;
            Q3=makeQuery(id+"F28.imprint","IMPRINT",FACE,{"disambiguationData":[TD([[makeQuery(id+"F28.imprint","IMPRINT",EDGE,{"derivedFrom":sQuery(id+"F28.wireOp",EDGE,"E84.sketch_text.stroke-41")}),-1.0]])]});
            var Q4;
            Q4=makeQuery(id+"F28.imprint","IMPRINT",FACE,{"disambiguationData":[TD([[makeQuery(id+"F28.imprint","IMPRINT",EDGE,{"derivedFrom":sQuery(id+"F28.wireOp",EDGE,"E84.sketch_text.stroke-53")}),-1.0]])]});
            var Q5;
            Q5=makeQuery(id+"F28.imprint","IMPRINT",FACE,{"disambiguationData":[TD([[makeQuery(id+"F28.imprint","IMPRINT",EDGE,{"derivedFrom":sQuery(id+"F28.wireOp",EDGE,"E84.sketch_text.stroke-71")}),-1.0]])]});
            var Q6;
            Q6=makeQuery(id+"F28.imprint","IMPRINT",FACE,{"disambiguationData":[TD([[makeQuery(id+"F28.imprint","IMPRINT",EDGE,{"derivedFrom":sQuery(id+"F28.wireOp",EDGE,"E84.sketch_text.stroke-96")}),-1.0]])]});
            var Q7;
            Q7=makeQuery(id+"F28.imprint","IMPRINT",FACE,{"disambiguationData":[TD([[makeQuery(id+"F28.imprint","IMPRINT",EDGE,{"derivedFrom":sQuery(id+"F28.wireOp",EDGE,"E84.sketch_text.stroke-108")}),-1.0]])]});
            var Q8;
            Q8=makeQuery(id+"F28.imprint","IMPRINT",FACE,{"disambiguationData":[TD([[makeQuery(id+"F28.imprint","IMPRINT",EDGE,{"derivedFrom":sQuery(id+"F28.wireOp",EDGE,"E84.sketch_text.stroke-33")}),-1.0]])]});
            var Q9;
            Q9=makeQuery(id+"F28.imprint","IMPRINT",FACE,{"disambiguationData":[TD([[makeQuery(id+"F28.imprint","IMPRINT",EDGE,{"derivedFrom":sQuery(id+"F28.wireOp",EDGE,"E84.sketch_text.stroke-110")}),-1.0]])]});
            extrude(context, id + "F29", {"entities" : qUnion([Q0, Q1, Q2, Q3, Q4, Q5, Q6, Q7, Q8, Q9]), "operationType" : NewBodyOperationType.REMOVE, "oppositeDirection" : true, "depth" : 1.5 * mm});
        }
        {
            var Q0;
            Q0=makeQuery(id+"F26.imprint","IMPRINT",FACE,{"disambiguationData":[TD([[makeQuery(id+"F26.imprint","IMPRINT",EDGE,{"derivedFrom":sQuery(id+"F26.wireOp",EDGE,"E78.sketch_text.stroke-0")}),-1.0]])]});
            var Q1;
            Q1=makeQuery(id+"F26.imprint","IMPRINT",FACE,{"disambiguationData":[TD([[makeQuery(id+"F26.imprint","IMPRINT",EDGE,{"derivedFrom":sQuery(id+"F26.wireOp",EDGE,"E78.sketch_text.stroke-15")}),-1.0]])]});
            var Q2;
            Q2=makeQuery(id+"F26.imprint","IMPRINT",FACE,{"disambiguationData":[TD([[makeQuery(id+"F26.imprint","IMPRINT",EDGE,{"derivedFrom":sQuery(id+"F26.wireOp",EDGE,"E78.sketch_text.stroke-31")}),-1.0]])]});
            var Q3;
            Q3=makeQuery(id+"F26.imprint","IMPRINT",FACE,{"disambiguationData":[TD([[makeQuery(id+"F26.imprint","IMPRINT",EDGE,{"derivedFrom":sQuery(id+"F26.wireOp",EDGE,"E78.sketch_text.stroke-40")}),-1.0]])]});
            var Q4;
            Q4=makeQuery(id+"F26.imprint","IMPRINT",FACE,{"disambiguationData":[TD([[makeQuery(id+"F26.imprint","IMPRINT",EDGE,{"derivedFrom":sQuery(id+"F26.wireOp",EDGE,"E78.sketch_text.stroke-52")}),-1.0]])]});
            var Q5;
            Q5=makeQuery(id+"F26.imprint","IMPRINT",FACE,{"disambiguationData":[TD([[makeQuery(id+"F26.imprint","IMPRINT",EDGE,{"derivedFrom":sQuery(id+"F26.wireOp",EDGE,"E78.sketch_text.stroke-70")}),-1.0]])]});
            var Q6;
            Q6=makeQuery(id+"F26.imprint","IMPRINT",FACE,{"disambiguationData":[TD([[makeQuery(id+"F26.imprint","IMPRINT",EDGE,{"derivedFrom":sQuery(id+"F26.wireOp",EDGE,"E78.sketch_text.stroke-95")}),-1.0]])]});
            var Q7;
            Q7=makeQuery(id+"F26.imprint","IMPRINT",FACE,{"disambiguationData":[TD([[makeQuery(id+"F26.imprint","IMPRINT",EDGE,{"derivedFrom":sQuery(id+"F26.wireOp",EDGE,"E78.sketch_text.stroke-107")}),-1.0]])]});
            var Q8;
            Q8=makeQuery(id+"F26.imprint","IMPRINT",FACE,{"disambiguationData":[TD([[makeQuery(id+"F26.imprint","IMPRINT",EDGE,{"derivedFrom":sQuery(id+"F26.wireOp",EDGE,"E78.sketch_text.stroke-117")}),-1.0]])]});
            extrude(context, id + "F30", {"entities" : qUnion([Q0, Q1, Q2, Q3, Q4, Q5, Q6, Q7, Q8]), "operationType" : NewBodyOperationType.REMOVE, "oppositeDirection" : true, "depth" : 1.5 * mm});
        }
        {
            var Q0;
            Q0=makeQuery(id+"F24.imprint","IMPRINT",FACE,{"disambiguationData":[TD([[makeQuery(id+"F24.imprint","IMPRINT",EDGE,{"derivedFrom":sQuery(id+"F24.wireOp",EDGE,"E72.sketch_text.stroke-0")}),-1.0]])]});
            var Q1;
            Q1=makeQuery(id+"F24.imprint","IMPRINT",FACE,{"disambiguationData":[TD([[makeQuery(id+"F24.imprint","IMPRINT",EDGE,{"derivedFrom":sQuery(id+"F24.wireOp",EDGE,"E72.sketch_text.stroke-16")}),-1.0]])]});
            var Q2;
            Q2=makeQuery(id+"F24.imprint","IMPRINT",FACE,{"disambiguationData":[TD([[makeQuery(id+"F24.imprint","IMPRINT",EDGE,{"derivedFrom":sQuery(id+"F24.wireOp",EDGE,"E72.sketch_text.stroke-31")}),-1.0]])]});
            var Q3;
            Q3=makeQuery(id+"F24.imprint","IMPRINT",FACE,{"disambiguationData":[TD([[makeQuery(id+"F24.imprint","IMPRINT",EDGE,{"derivedFrom":sQuery(id+"F24.wireOp",EDGE,"E72.sketch_text.stroke-39")}),-1.0]])]});
            var Q4;
            Q4=makeQuery(id+"F24.imprint","IMPRINT",FACE,{"disambiguationData":[TD([[makeQuery(id+"F24.imprint","IMPRINT",EDGE,{"derivedFrom":sQuery(id+"F24.wireOp",EDGE,"E72.sketch_text.stroke-55")}),-1.0]])]});
            var Q5;
            Q5=makeQuery(id+"F24.imprint","IMPRINT",FACE,{"disambiguationData":[TD([[makeQuery(id+"F24.imprint","IMPRINT",EDGE,{"derivedFrom":sQuery(id+"F24.wireOp",EDGE,"E72.sketch_text.stroke-80")}),-1.0]])]});
            var Q6;
            Q6=makeQuery(id+"F24.imprint","IMPRINT",FACE,{"disambiguationData":[TD([[makeQuery(id+"F24.imprint","IMPRINT",EDGE,{"derivedFrom":sQuery(id+"F24.wireOp",EDGE,"E72.sketch_text.stroke-92")}),-1.0]])]});
            var Q7;
            Q7=makeQuery(id+"F24.imprint","IMPRINT",FACE,{"disambiguationData":[TD([[makeQuery(id+"F24.imprint","IMPRINT",EDGE,{"derivedFrom":sQuery(id+"F24.wireOp",EDGE,"E72.sketch_text.stroke-110")}),-1.0]])]});
            extrude(context, id + "F31", {"entities" : qUnion([Q0, Q1, Q2, Q3, Q4, Q5, Q6, Q7]), "operationType" : NewBodyOperationType.REMOVE, "oppositeDirection" : true, "depth" : 1.5 * mm});
        }
        {
            var Q0;
            Q0=makeQuery(id+"F22.imprint","IMPRINT",FACE,{"disambiguationData":[TD([[makeQuery(id+"F22.imprint","IMPRINT",EDGE,{"derivedFrom":sQuery(id+"F22.wireOp",EDGE,"E67.sketch_text.stroke-0")}),-1.0]])]});
            var Q1;
            Q1=makeQuery(id+"F22.imprint","IMPRINT",FACE,{"disambiguationData":[TD([[makeQuery(id+"F22.imprint","IMPRINT",EDGE,{"derivedFrom":sQuery(id+"F22.wireOp",EDGE,"E67.sketch_text.stroke-25")}),-1.0]])]});
            var Q2;
            Q2=makeQuery(id+"F22.imprint","IMPRINT",FACE,{"disambiguationData":[TD([[makeQuery(id+"F22.imprint","IMPRINT",EDGE,{"derivedFrom":sQuery(id+"F22.wireOp",EDGE,"E67.sketch_text.stroke-37")}),-1.0]])]});
            var Q3;
            Q3=makeQuery(id+"F22.imprint","IMPRINT",FACE,{"disambiguationData":[TD([[makeQuery(id+"F22.imprint","IMPRINT",EDGE,{"derivedFrom":sQuery(id+"F22.wireOp",EDGE,"E67.sketch_text.stroke-52")}),-1.0]])]});
            var Q4;
            Q4=makeQuery(id+"F22.imprint","IMPRINT",FACE,{"disambiguationData":[TD([[makeQuery(id+"F22.imprint","IMPRINT",EDGE,{"derivedFrom":sQuery(id+"F22.wireOp",EDGE,"E67.sketch_text.stroke-60")}),-1.0]])]});
            var Q5;
            Q5=makeQuery(id+"F22.imprint","IMPRINT",FACE,{"disambiguationData":[TD([[makeQuery(id+"F22.imprint","IMPRINT",EDGE,{"derivedFrom":sQuery(id+"F22.wireOp",EDGE,"E67.sketch_text.stroke-72")}),-1.0]])]});
            var Q6;
            Q6=makeQuery(id+"F22.imprint","IMPRINT",FACE,{"disambiguationData":[TD([[makeQuery(id+"F22.imprint","IMPRINT",EDGE,{"derivedFrom":sQuery(id+"F22.wireOp",EDGE,"E67.sketch_text.stroke-90")}),-1.0]])]});
            var Q7;
            Q7=makeQuery(id+"F22.imprint","IMPRINT",FACE,{"disambiguationData":[TD([[makeQuery(id+"F22.imprint","IMPRINT",EDGE,{"derivedFrom":sQuery(id+"F22.wireOp",EDGE,"E67.sketch_text.stroke-115")}),-1.0]])]});
            var Q8;
            Q8=makeQuery(id+"F22.imprint","IMPRINT",FACE,{"disambiguationData":[TD([[makeQuery(id+"F22.imprint","IMPRINT",EDGE,{"derivedFrom":sQuery(id+"F22.wireOp",EDGE,"E67.sketch_text.stroke-127")}),-1.0]])]});
            var Q9;
            Q9=makeQuery(id+"F22.imprint","IMPRINT",FACE,{"disambiguationData":[TD([[makeQuery(id+"F22.imprint","IMPRINT",EDGE,{"derivedFrom":sQuery(id+"F22.wireOp",EDGE,"E67.sketch_text.stroke-137")}),-1.0]])]});
            extrude(context, id + "F32", {"entities" : qUnion([Q0, Q1, Q2, Q3, Q4, Q5, Q6, Q7, Q8, Q9]), "operationType" : NewBodyOperationType.REMOVE, "oppositeDirection" : true, "depth" : 1.5 * mm});
        }
        {
            var Q0;
            Q0=makeQuery(id+"F20.imprint","IMPRINT",FACE,{"disambiguationData":[TD([[makeQuery(id+"F20.imprint","IMPRINT",EDGE,{"derivedFrom":sQuery(id+"F20.wireOp",EDGE,"E57.sketch_text.stroke-0")}),-1.0]])]});
            var Q1;
            Q1=makeQuery(id+"F20.imprint","IMPRINT",FACE,{"disambiguationData":[TD([[makeQuery(id+"F20.imprint","IMPRINT",EDGE,{"derivedFrom":sQuery(id+"F20.wireOp",EDGE,"E57.sketch_text.stroke-13")}),-1.0]])]});
            var Q2;
            Q2=makeQuery(id+"F20.imprint","IMPRINT",FACE,{"disambiguationData":[TD([[makeQuery(id+"F20.imprint","IMPRINT",EDGE,{"derivedFrom":sQuery(id+"F20.wireOp",EDGE,"E57.sketch_text.stroke-27")}),-1.0]])]});
            var Q3;
            Q3=makeQuery(id+"F20.imprint","IMPRINT",FACE,{"disambiguationData":[TD([[makeQuery(id+"F20.imprint","IMPRINT",EDGE,{"derivedFrom":sQuery(id+"F20.wireOp",EDGE,"E57.sketch_text.stroke-47")}),-1.0]])]});
            var Q4;
            Q4=makeQuery(id+"F20.imprint","IMPRINT",FACE,{"disambiguationData":[TD([[makeQuery(id+"F20.imprint","IMPRINT",EDGE,{"derivedFrom":sQuery(id+"F20.wireOp",EDGE,"E57.sketch_text.stroke-61")}),-1.0]])]});
            var Q5;
            Q5=makeQuery(id+"F20.imprint","IMPRINT",FACE,{"disambiguationData":[TD([[makeQuery(id+"F20.imprint","IMPRINT",EDGE,{"derivedFrom":sQuery(id+"F20.wireOp",EDGE,"E57.sketch_text.stroke-86")}),-1.0]])]});
            var Q6;
            Q6=makeQuery(id+"F20.imprint","IMPRINT",FACE,{"disambiguationData":[TD([[makeQuery(id+"F20.imprint","IMPRINT",EDGE,{"derivedFrom":sQuery(id+"F20.wireOp",EDGE,"E57.sketch_text.stroke-74")}),-1.0]])]});
            extrude(context, id + "F33", {"entities" : qUnion([Q0, Q1, Q2, Q3, Q4, Q5, Q6]), "operationType" : NewBodyOperationType.REMOVE, "oppositeDirection" : true, "depth" : 1.5 * mm});
        }
        {
            var Q0;
            Q0=makeQuery(id+"F18.imprint","IMPRINT",FACE,{"disambiguationData":[TD([[makeQuery(id+"F18.imprint","IMPRINT",EDGE,{"derivedFrom":sQuery(id+"F18.wireOp",EDGE,"E48.sketch_text.stroke-0")}),-1.0]])]});
            var Q1;
            Q1=makeQuery(id+"F18.imprint","IMPRINT",FACE,{"disambiguationData":[TD([[makeQuery(id+"F18.imprint","IMPRINT",EDGE,{"derivedFrom":sQuery(id+"F18.wireOp",EDGE,"E48.sketch_text.stroke-10")}),-1.0]])]});
            var Q2;
            Q2=makeQuery(id+"F18.imprint","IMPRINT",FACE,{"disambiguationData":[TD([[makeQuery(id+"F18.imprint","IMPRINT",EDGE,{"derivedFrom":sQuery(id+"F18.wireOp",EDGE,"E48.sketch_text.stroke-24")}),-1.0]])]});
            var Q3;
            Q3=makeQuery(id+"F18.imprint","IMPRINT",FACE,{"disambiguationData":[TD([[makeQuery(id+"F18.imprint","IMPRINT",EDGE,{"derivedFrom":sQuery(id+"F18.wireOp",EDGE,"E48.sketch_text.stroke-30")}),-1.0]])]});
            var Q4;
            Q4=makeQuery(id+"F18.imprint","IMPRINT",FACE,{"disambiguationData":[TD([[makeQuery(id+"F18.imprint","IMPRINT",EDGE,{"derivedFrom":sQuery(id+"F18.wireOp",EDGE,"E48.sketch_text.stroke-34")}),-1.0]])]});
            extrude(context, id + "F34", {"entities" : qUnion([Q0, Q1, Q2, Q3, Q4]), "operationType" : NewBodyOperationType.REMOVE, "oppositeDirection" : true, "depth" : 1.5 * mm});
        }
        {
            var Q0;
            Q0=makeQuery(id+"F16.imprint","IMPRINT",FACE,{"disambiguationData":[TD([[makeQuery(id+"F16.imprint","IMPRINT",EDGE,{"derivedFrom":sQuery(id+"F16.wireOp",EDGE,"E40.sketch_text.stroke-0")}),-1.0]])]});
            var Q1;
            Q1=makeQuery(id+"F16.imprint","IMPRINT",FACE,{"disambiguationData":[TD([[makeQuery(id+"F16.imprint","IMPRINT",EDGE,{"derivedFrom":sQuery(id+"F16.wireOp",EDGE,"E40.sketch_text.stroke-10")}),-1.0]])]});
            var Q2;
            Q2=makeQuery(id+"F16.imprint","IMPRINT",FACE,{"disambiguationData":[TD([[makeQuery(id+"F16.imprint","IMPRINT",EDGE,{"derivedFrom":sQuery(id+"F16.wireOp",EDGE,"E40.sketch_text.stroke-24")}),-1.0]])]});
            var Q3;
            Q3=makeQuery(id+"F16.imprint","IMPRINT",FACE,{"disambiguationData":[TD([[makeQuery(id+"F16.imprint","IMPRINT",EDGE,{"derivedFrom":sQuery(id+"F16.wireOp",EDGE,"E40.sketch_text.stroke-39")}),-1.0]])]});
            var Q4;
            Q4=makeQuery(id+"F16.imprint","IMPRINT",FACE,{"disambiguationData":[TD([[makeQuery(id+"F16.imprint","IMPRINT",EDGE,{"derivedFrom":sQuery(id+"F16.wireOp",EDGE,"E40.sketch_text.stroke-43")}),-1.0]])]});
            extrude(context, id + "F35", {"entities" : qUnion([Q0, Q1, Q2, Q3, Q4]), "operationType" : NewBodyOperationType.REMOVE, "oppositeDirection" : true, "depth" : 1.5 * mm});
        }
        {
            var Q0;
            Q0=makeQuery(id+"F14.imprint","IMPRINT",FACE,{"disambiguationData":[TD([[makeQuery(id+"F14.imprint","IMPRINT",EDGE,{"derivedFrom":sQuery(id+"F14.wireOp",EDGE,"E33.sketch_text.stroke-0")}),-1.0]])]});
            var Q1;
            Q1=makeQuery(id+"F14.imprint","IMPRINT",FACE,{"disambiguationData":[TD([[makeQuery(id+"F14.imprint","IMPRINT",EDGE,{"derivedFrom":sQuery(id+"F14.wireOp",EDGE,"E33.sketch_text.stroke-18")}),-1.0]])]});
            var Q2;
            Q2=makeQuery(id+"F14.imprint","IMPRINT",FACE,{"disambiguationData":[TD([[makeQuery(id+"F14.imprint","IMPRINT",EDGE,{"derivedFrom":sQuery(id+"F14.wireOp",EDGE,"E33.sketch_text.stroke-31")}),-1.0]])]});
            var Q3;
            Q3=makeQuery(id+"F14.imprint","IMPRINT",FACE,{"disambiguationData":[TD([[makeQuery(id+"F14.imprint","IMPRINT",EDGE,{"derivedFrom":sQuery(id+"F14.wireOp",EDGE,"E33.sketch_text.stroke-40")}),-1.0]])]});
            extrude(context, id + "F36", {"entities" : qUnion([Q0, Q1, Q2, Q3]), "operationType" : NewBodyOperationType.REMOVE, "oppositeDirection" : true, "depth" : 1.5 * mm});
        }
    });
